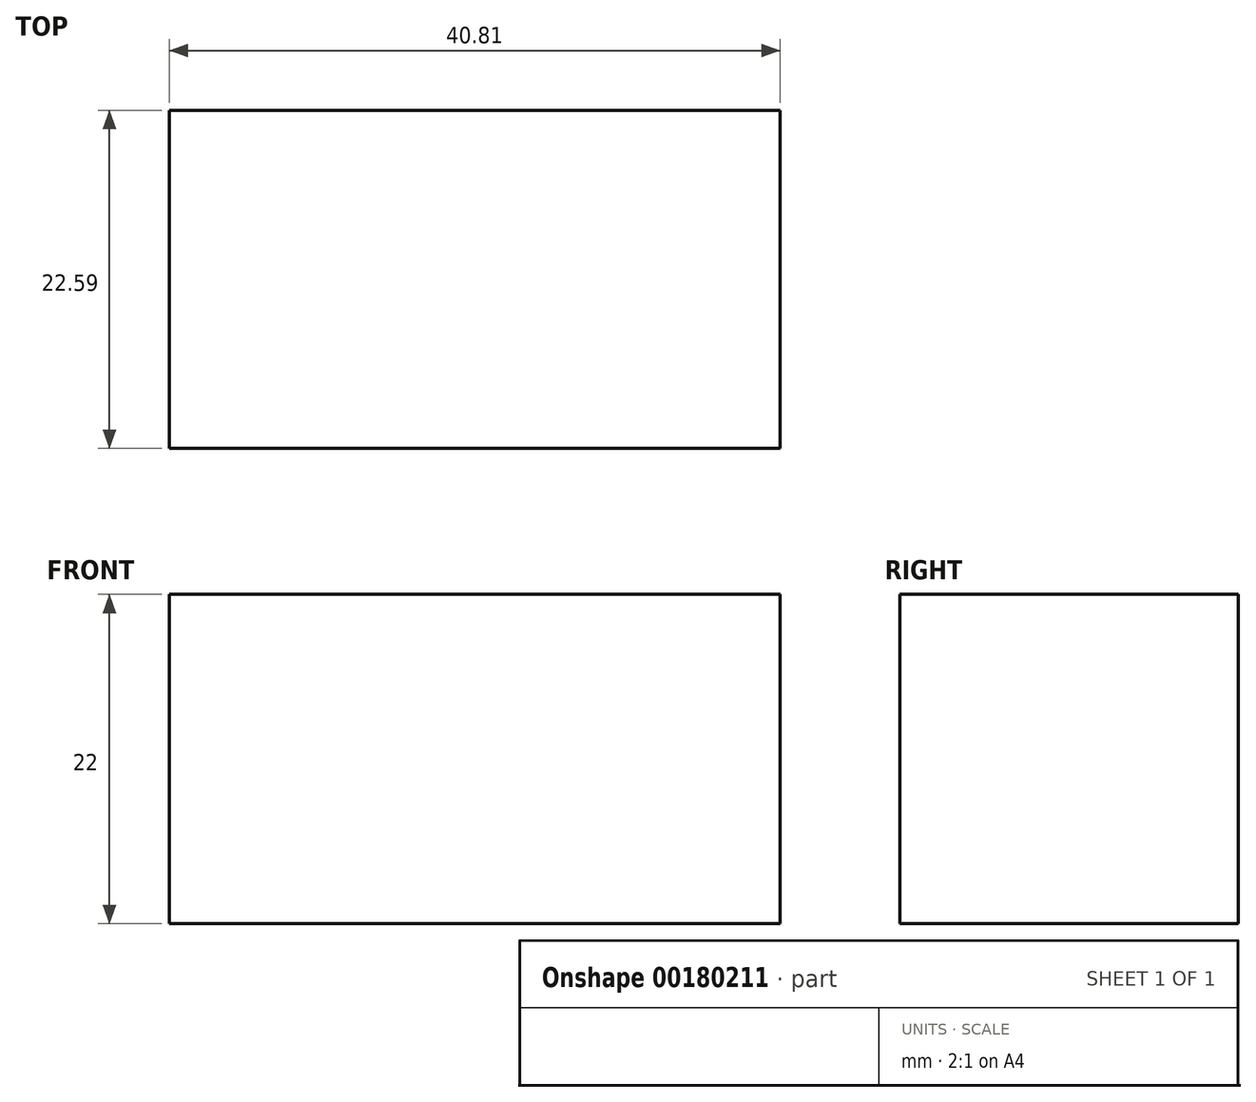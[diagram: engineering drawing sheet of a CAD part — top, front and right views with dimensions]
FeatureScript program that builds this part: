
annotation { "Feature Type Name" : "Feature", "Feature Type Description" : "" }
export const myFeature = defineFeature(function(context is Context, id is Id, definition is map)
    precondition{}
    {
        {
            var Q0;
            Q0=qCreatedBy(makeId("Top.planeOp"),FACE);
            var sketch = newSketch(context, id + "F0", { "sketchPlane" : qUnion([Q0])});
            skLineSegment(sketch, "E0.bottom", {"start": v(-40.8, 16.3) * mm, "end": v(0, 16.3) * mm});
            skLineSegment(sketch, "E0.top", {"start": v(-40.8, 38.89) * mm, "end": v(0, 38.89) * mm});
            skLineSegment(sketch, "E0.left", {"start": v(-40.8, 16.3) * mm, "end": v(-40.8, 38.89) * mm});
            skLineSegment(sketch, "E0.right", {"start": v(0, 16.3) * mm, "end": v(0, 38.89) * mm});
            skSolve(sketch);
        }
        {
            var Q0;
            Q0=makeQuery(id+"F0.imprint","IMPRINT",FACE,{"disambiguationData":[TD([[makeQuery(id+"F0.imprint","IMPRINT",EDGE,{"derivedFrom":sQuery(id+"F0.wireOp",EDGE,"E0.bottom")}),1.0]])]});
            extrude(context, id + "F1", {"entities" : qUnion([Q0]), "endBound" : BoundingType.SYMMETRIC, "depth" : 22 * mm});
        }
    });
